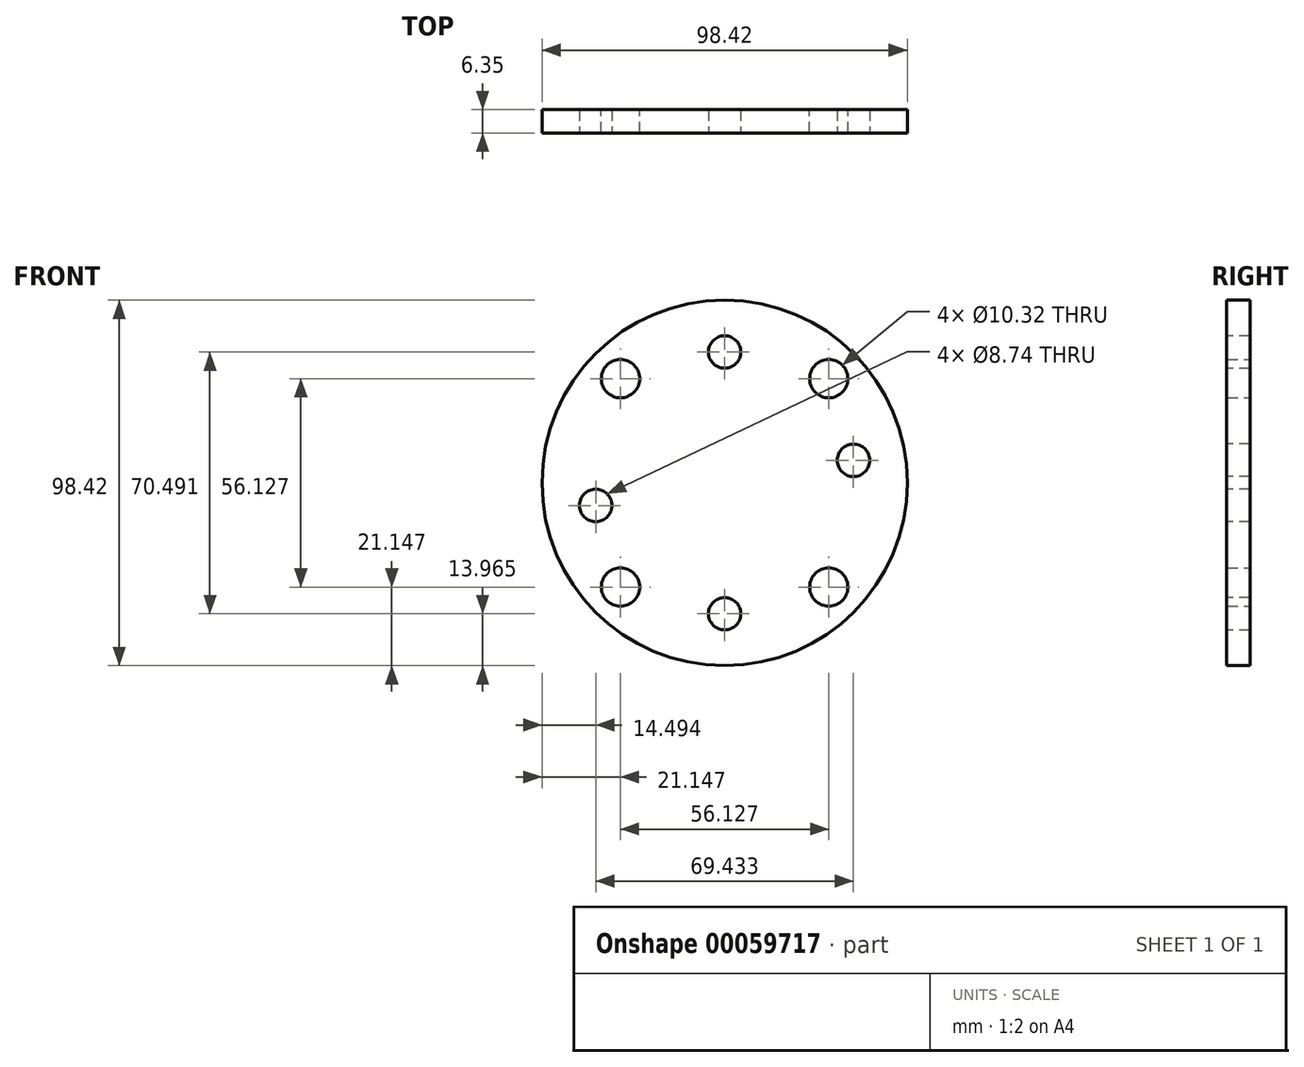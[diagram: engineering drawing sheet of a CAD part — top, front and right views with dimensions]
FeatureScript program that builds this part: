
annotation { "Feature Type Name" : "Feature", "Feature Type Description" : "" }
export const myFeature = defineFeature(function(context is Context, id is Id, definition is map)
    precondition{}
    {
        {
            var Q0;
            Q0=qCreatedBy(makeId("Front.planeOp"),FACE);
            var sketch = newSketch(context, id + "F0", { "sketchPlane" : qUnion([Q0])});
            skCircle(sketch, "E0", {"center": v(0, 0) * mm, "radius": 49.21 * mm});
            skCircle(sketch, "E1.cCircle", {"center": v(0, 0) * mm, "radius": 39.69 * mm, "construction": true});
            skLineSegment(sketch, "E1.0", {"start": v(-28.06, 28.06) * mm, "end": v(28.06, 28.06) * mm, "construction": true});
            skLineSegment(sketch, "E1.1", {"start": v(28.06, 28.06) * mm, "end": v(28.06, -28.06) * mm, "construction": true});
            skLineSegment(sketch, "E1.2", {"start": v(28.06, -28.06) * mm, "end": v(-28.06, -28.06) * mm, "construction": true});
            skLineSegment(sketch, "E1.3", {"start": v(-28.06, -28.06) * mm, "end": v(-28.06, 28.06) * mm, "construction": true});
            skCircle(sketch, "E2", {"center": v(-28.06, 28.06) * mm, "radius": 5.16 * mm});
            skCircle(sketch, "E3", {"center": v(28.06, 28.06) * mm, "radius": 5.16 * mm});
            skCircle(sketch, "E4", {"center": v(28.06, -28.06) * mm, "radius": 5.16 * mm});
            skCircle(sketch, "E5", {"center": v(-28.06, -28.06) * mm, "radius": 5.16 * mm});
            skSolve(sketch);
        }
        {
            var Q0;
            Q0 = qSketchRegion(id + "F0", true);
            extrude(context, id + "F1", {"entities" : qUnion([Q0]), "depth" : 6.35 * mm});
        }
        {
            var Q0;
            Q0=makeQuery(id+"F1.opExtrude","CAP_FACE",FACE,{"disambiguationData":[OSD([sQuery(id+"F0.wireOp",EDGE,"E0"),sQuery(id+"F0.wireOp",EDGE,"E2"),sQuery(id+"F0.wireOp",EDGE,"E3"),sQuery(id+"F0.wireOp",EDGE,"E4"),sQuery(id+"F0.wireOp",EDGE,"E5")])],"isStart":false});
            var sketch = newSketch(context, id + "F2", { "sketchPlane" : qUnion([Q0])});
            skLineSegment(sketch, "E6.rect.bottom", {"start": v(0, 35.25) * mm, "end": v(-34.72, -6.08) * mm});
            skLineSegment(sketch, "E6.rect.top", {"start": v(34.72, 6.08) * mm, "end": v(0, -35.25) * mm});
            skLineSegment(sketch, "E6.rect.left", {"start": v(0, 35.25) * mm, "end": v(34.72, 6.08) * mm});
            skLineSegment(sketch, "E6.rect.right", {"start": v(-34.72, -6.08) * mm, "end": v(0, -35.25) * mm});
            skPoint(sketch, "E6.rect.middle", {"position": v(0, 0) * mm});
            skSolve(sketch);
        }
        {
            var Q0;
            Q0=sQuery(id+"F2.wireOp",VERTEX,"E6.rect.left.start");
            var Q1;
            Q1=sQuery(id+"F2.wireOp",VERTEX,"E6.rect.left.end");
            var Q2;
            Q2=sQuery(id+"F2.wireOp",VERTEX,"E6.rect.top.end");
            var Q3;
            Q3=sQuery(id+"F2.wireOp",VERTEX,"E6.rect.right.start");
            var Q4;
            Q4=makeQuery(id+"F1.opExtrude","SWEPT_BODY",BODY,{"disambiguationData":[OSD([sQuery(id+"F0.wireOp",EDGE,"E0"),sQuery(id+"F0.wireOp",EDGE,"E2"),sQuery(id+"F0.wireOp",EDGE,"E3"),sQuery(id+"F0.wireOp",EDGE,"E4"),sQuery(id+"F0.wireOp",EDGE,"E5")])]});
            hole(context, id + "F3", {"style" : HoleStyle.SIMPLE, "holeDiameter" : 8.74 * mm, "endStyle" : HoleEndStyle.THROUGH, "locations" : qUnion([Q0, Q1, Q2, Q3]), "scope" : qUnion([Q4])});
        }
    });
